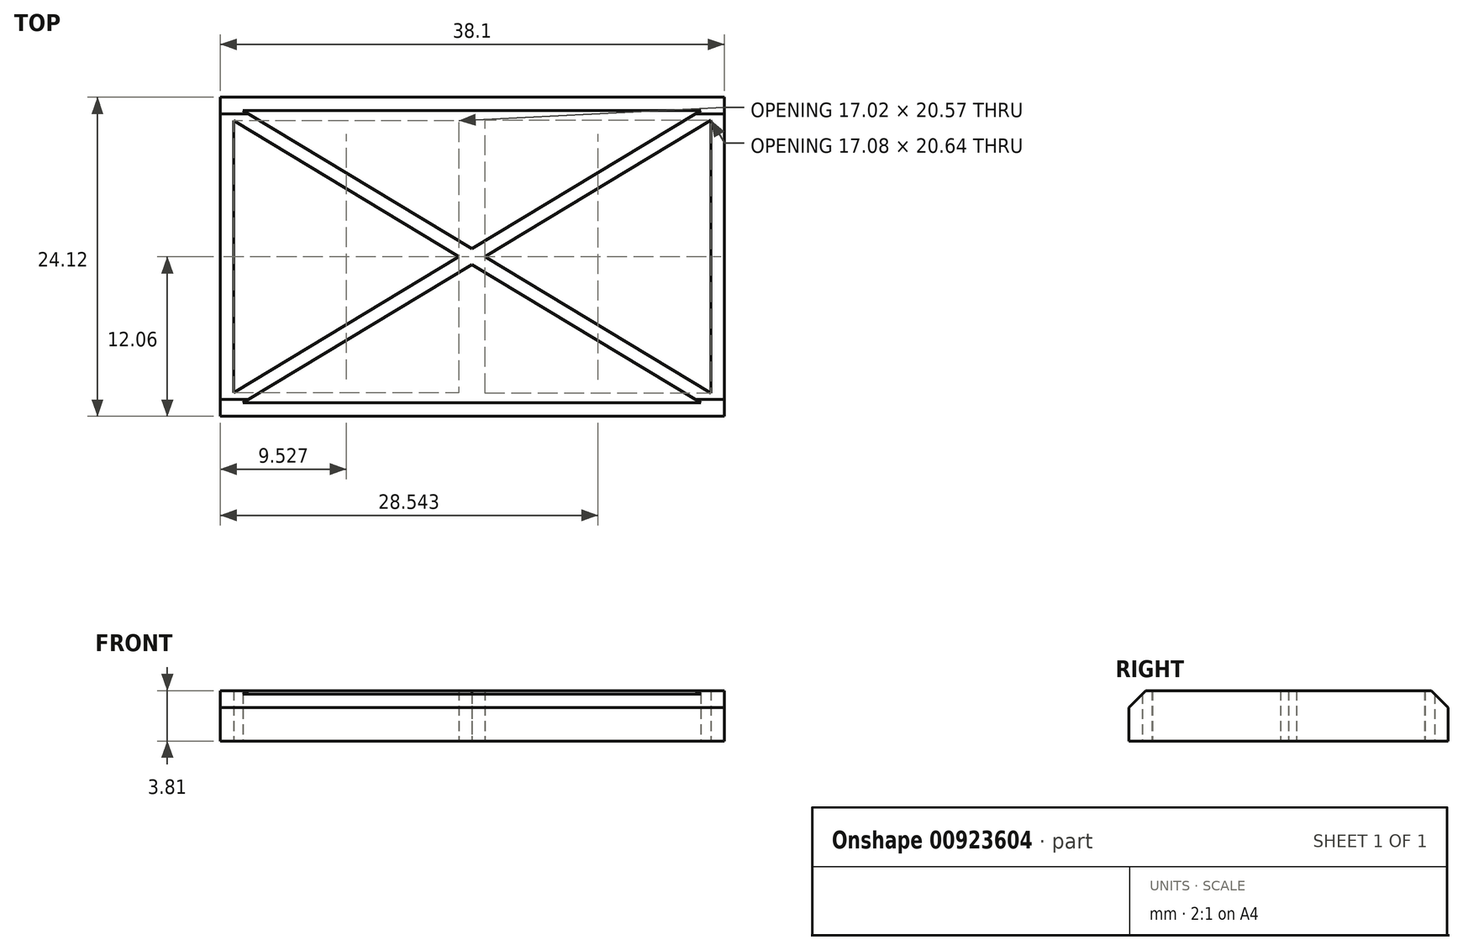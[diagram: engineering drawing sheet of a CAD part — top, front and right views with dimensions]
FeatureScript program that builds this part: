
annotation { "Feature Type Name" : "Feature", "Feature Type Description" : "" }
export const myFeature = defineFeature(function(context is Context, id is Id, definition is map)
    precondition{}
    {
        {
            var Q0;
            Q0=qCreatedBy(makeId("Top.planeOp"),FACE);
            var sketch = newSketch(context, id + "F0", { "sketchPlane" : qUnion([Q0])});
            skLineSegment(sketch, "E0.bottom", {"start": v(19.05, 12.06) * mm, "end": v(-19.05, 12.06) * mm});
            skLineSegment(sketch, "E0.top", {"start": v(19.05, -12.07) * mm, "end": v(-19.05, -12.07) * mm});
            skLineSegment(sketch, "E0.left", {"start": v(19.05, 12.06) * mm, "end": v(19.05, -12.07) * mm});
            skLineSegment(sketch, "E0.right", {"start": v(-19.05, 12.06) * mm, "end": v(-19.05, -12.07) * mm});
            skPoint(sketch, "E0.middle", {"position": v(0, 0) * mm});
            skLineSegment(sketch, "E1.bottom", {"start": v(17.27, 11.05) * mm, "end": v(-17.33, 11.05) * mm});
            skLineSegment(sketch, "E1.top", {"start": v(17.27, -11.05) * mm, "end": v(-17.33, -11.05) * mm});
            skLineSegment(sketch, "E1.left", {"start": v(18.03, 10.32) * mm, "end": v(18.03, -10.32) * mm});
            skLineSegment(sketch, "E1.right", {"start": v(-18.03, 10.29) * mm, "end": v(-18.03, -10.29) * mm});
            skLineSegment(sketch, "E2", {"start": v(-18.03, -10.29) * mm, "end": v(-1.01, 0) * mm});
            skLineSegment(sketch, "E3", {"start": v(18.03, 10.32) * mm, "end": v(0.95, 0) * mm});
            skPoint(sketch, "E4.orphan", {"position": v(-18.03, -11.05) * mm});
            skPoint(sketch, "E5.orphan", {"position": v(18.03, 11.05) * mm});
            skLineSegment(sketch, "E6.MirrorCS", {"start": v(-18.03, 10.29) * mm, "end": v(-1.01, 0) * mm});
            skLineSegment(sketch, "E7.MirrorCS", {"start": v(18.03, -10.32) * mm, "end": v(0.95, 0) * mm});
            skPoint(sketch, "E8.orphan", {"position": v(-18.03, 11.05) * mm});
            skPoint(sketch, "E9.orphan", {"position": v(18.03, -11.05) * mm});
            skLineSegment(sketch, "E10.trimOffspring", {"start": v(-0.03, 0.6) * mm, "end": v(17.27, 11.05) * mm});
            skLineSegment(sketch, "E11.trimOffspring", {"start": v(-0.03, 0.6) * mm, "end": v(-17.33, 11.05) * mm});
            skLineSegment(sketch, "E12.trimOffspring", {"start": v(-0.03, -0.6) * mm, "end": v(-17.33, -11.05) * mm});
            skLineSegment(sketch, "E13.trimOffspring", {"start": v(-0.03, -0.6) * mm, "end": v(17.27, -11.05) * mm});
            skSolve(sketch);
        }
        {
            var Q0;
            Q0 = qSketchRegion(id + "F0", true);
            extrude(context, id + "F1", {"entities" : qUnion([Q0]), "depth" : 3.8 * mm, "offsetDistance" : 25.4 * mm});
        }
        {
            var Q0;
            Q0=makeQuery(id+"F1.opExtrude","CAP_EDGE",EDGE,{"disambiguationData":[OSD([sQuery(id+"F0.wireOp",EDGE,"E0.top")])],"isStart":false});
            var Q1;
            Q1=makeQuery(id+"F1.opExtrude","CAP_EDGE",EDGE,{"disambiguationData":[OSD([sQuery(id+"F0.wireOp",EDGE,"E0.bottom")])],"isStart":false});
            chamfer(context, id + "F2", {"entities" : qUnion([Q0, Q1]), "width" : 1.27 * mm, "tangentPropagation" : true});
        }
    });
